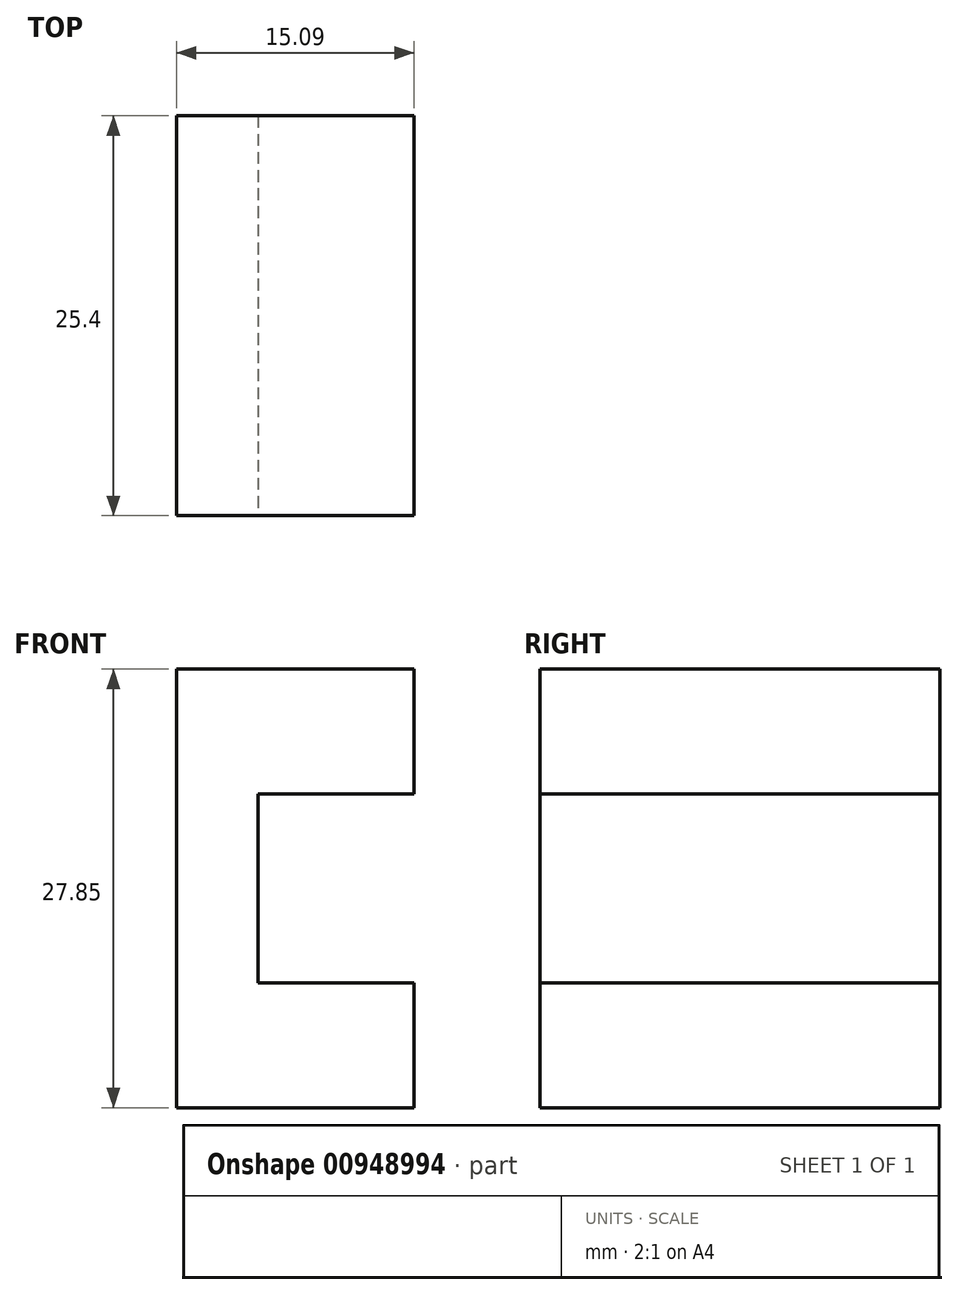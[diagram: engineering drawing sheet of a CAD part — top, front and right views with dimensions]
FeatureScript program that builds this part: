
annotation { "Feature Type Name" : "Feature", "Feature Type Description" : "" }
export const myFeature = defineFeature(function(context is Context, id is Id, definition is map)
    precondition{}
    {
        {
            var Q0;
            Q0=qCreatedBy(makeId("Front.planeOp"),FACE);
            var sketch = newSketch(context, id + "F0", { "sketchPlane" : qUnion([Q0])});
            skLineSegment(sketch, "E0.bottom", {"start": v(0, 0) * mm, "end": v(15.1, 0) * mm});
            skLineSegment(sketch, "E0.top", {"start": v(0, 27.85) * mm, "end": v(15.1, 27.85) * mm});
            skLineSegment(sketch, "E0.left", {"start": v(0, 0) * mm, "end": v(0, 27.85) * mm});
            skLineSegment(sketch, "E0.right", {"start": v(15.1, 0) * mm, "end": v(15.1, 27.85) * mm});
            skSolve(sketch);
        }
        {
            var Q0;
            Q0=makeQuery(id+"F0.imprint","IMPRINT",FACE,{"disambiguationData":[TD([[makeQuery(id+"F0.imprint","IMPRINT",EDGE,{"derivedFrom":sQuery(id+"F0.wireOp",EDGE,"E0.bottom")}),1.0]])]});
            extrude(context, id + "F1", {"entities" : qUnion([Q0]), "depth" : 25.4 * mm, "offsetDistance" : 25.4 * mm});
        }
        {
            var Q0;
            Q0=makeQuery(id+"F1.opExtrude","CAP_FACE",FACE,{"disambiguationData":[OSD([sQuery(id+"F0.wireOp",EDGE,"E0.bottom"),sQuery(id+"F0.wireOp",EDGE,"E0.top"),sQuery(id+"F0.wireOp",EDGE,"E0.left"),sQuery(id+"F0.wireOp",EDGE,"E0.right")])],"isStart":false});
            var sketch = newSketch(context, id + "F2", { "sketchPlane" : qUnion([Q0])});
            skLineSegment(sketch, "E1.bottom", {"start": v(5.17, 7.92) * mm, "end": v(25, 7.92) * mm});
            skLineSegment(sketch, "E1.top", {"start": v(5.17, 19.93) * mm, "end": v(25, 19.93) * mm});
            skLineSegment(sketch, "E1.left", {"start": v(5.17, 7.92) * mm, "end": v(5.17, 19.93) * mm});
            skLineSegment(sketch, "E1.right", {"start": v(25, 7.92) * mm, "end": v(25, 19.93) * mm});
            skPoint(sketch, "E1.middle", {"position": v(15.1, 13.93) * mm});
            skSolve(sketch);
        }
        {
            var Q0;
            {var subQ0=sQuery(id+"F2.wireOp",EDGE,"E1.left");Q0=makeQuery(id+"F2.imprint","IMPRINT",FACE,{"disambiguationData":[TD([[makeQuery(id+"F2.imprint","IMPRINT",EDGE,{"derivedFrom":subQ0}),-1.0]])]});}
            var Q1;
            {var subQ0=sQuery(id+"F2.wireOp",EDGE,"E1.right");Q1=makeQuery(id+"F2.imprint","IMPRINT",FACE,{"disambiguationData":[TD([[makeQuery(id+"F2.imprint","IMPRINT",EDGE,{"derivedFrom":subQ0}),1.0]])]});}
            extrude(context, id + "F3", {"entities" : qUnion([Q0, Q1]), "operationType" : NewBodyOperationType.REMOVE, "oppositeDirection" : true, "depth" : 25.4 * mm, "offsetDistance" : 25.4 * mm});
        }
        {
            var Q0;
            Q0=makeQuery(id+"F1.opExtrude","SWEPT_FACE",FACE,{"disambiguationData":[OSD([sQuery(id+"F0.wireOp",EDGE,"E0.top")])]});
            var sketch = newSketch(context, id + "F4", { "sketchPlane" : qUnion([Q0])});
            skLineSegment(sketch, "E2", {"start": v(5.17, -25.4) * mm, "end": v(5.17, 0) * mm});
            skPoint(sketch, "E2.endSnap0", {"position": v(7.55, 0) * mm});
            skLineSegment(sketch, "E3.bottom", {"start": v(5.17, -19.24) * mm, "end": v(25.02, -19.24) * mm});
            skLineSegment(sketch, "E3.top", {"start": v(5.17, -6.16) * mm, "end": v(25.02, -6.16) * mm});
            skLineSegment(sketch, "E3.left", {"start": v(5.17, -19.24) * mm, "end": v(5.17, -6.16) * mm});
            skLineSegment(sketch, "E3.right", {"start": v(25.02, -19.24) * mm, "end": v(25.02, -6.16) * mm});
            skPoint(sketch, "E3.middle", {"position": v(15.1, -12.7) * mm});
            skSolve(sketch);
        }
        {
            var Q0;
            {var subQ0=sQuery(id+"F4.wireOp",EDGE,"E3.right");Q0=makeQuery(id+"F4.imprint","IMPRINT",FACE,{"disambiguationData":[TD([[makeQuery(id+"F4.imprint","IMPRINT",EDGE,{"derivedFrom":subQ0}),1.0]])]});}
            var Q1;
            {var subQ0=sQuery(id+"F4.wireOp",EDGE,"E3.left");Q1=makeQuery(id+"F4.imprint","IMPRINT",FACE,{"disambiguationData":[TD([[makeQuery(id+"F4.imprint","IMPRINT",EDGE,{"derivedFrom":subQ0}),-1.0]])]});}
            extrude(context, id + "F5", {"entities" : qUnion([Q0, Q1]), "operationType" : NewBodyOperationType.REMOVE, "oppositeDirection" : true, "depth" : 67.54 * mm, "offsetDistance" : 25.4 * mm});
        }
    });
